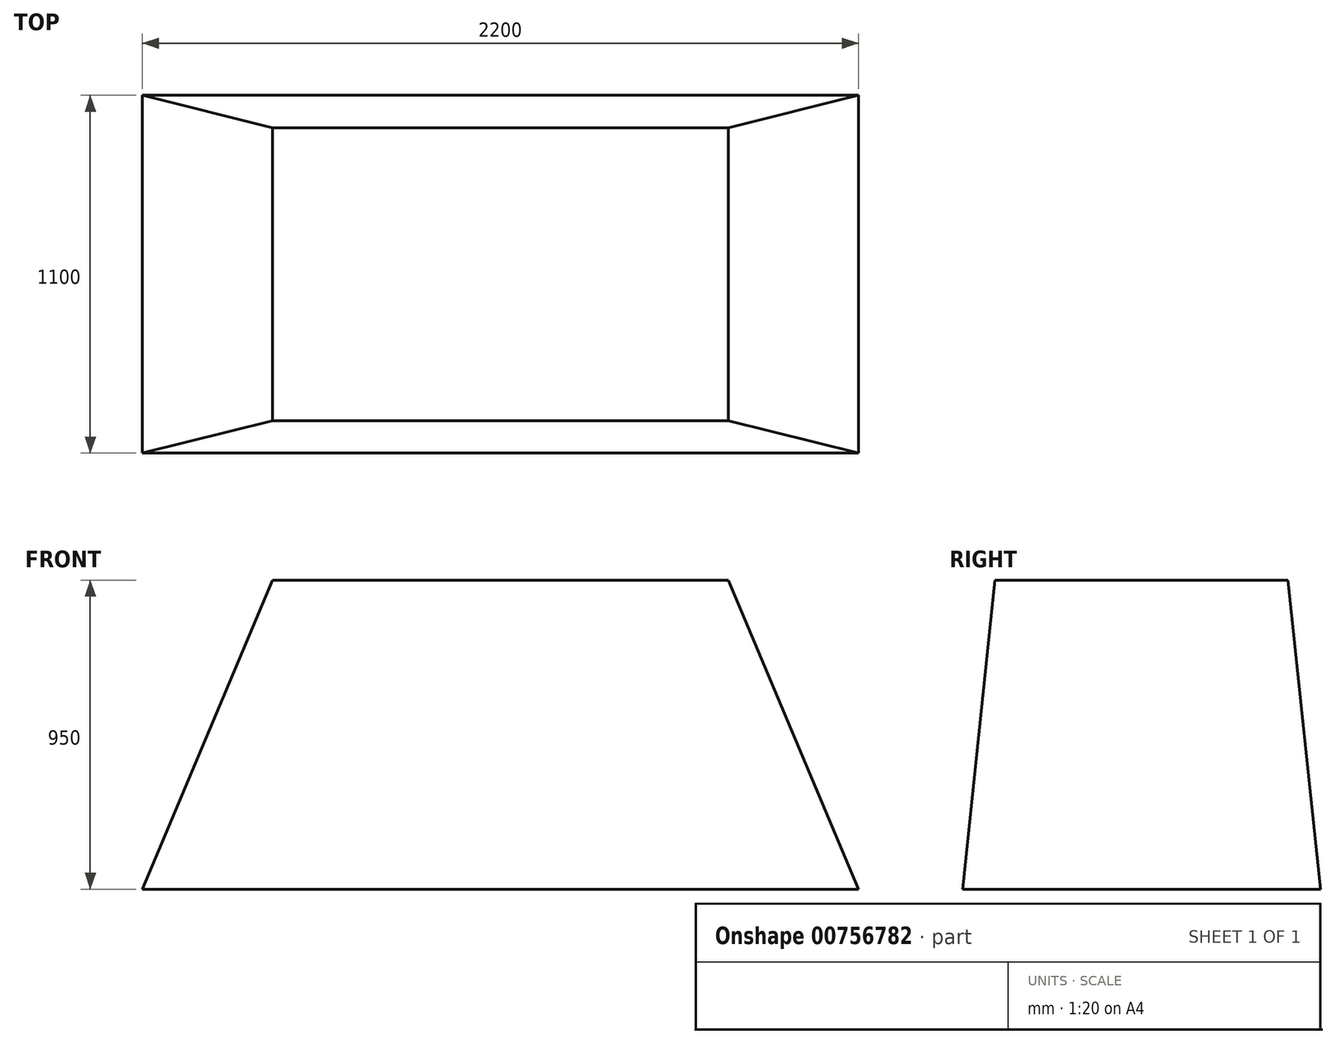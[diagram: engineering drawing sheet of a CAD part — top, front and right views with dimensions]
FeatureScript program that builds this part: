
annotation { "Feature Type Name" : "Feature", "Feature Type Description" : "" }
export const myFeature = defineFeature(function(context is Context, id is Id, definition is map)
    precondition{}
    {
        {
            var Q0;
            Q0=qCreatedBy(makeId("Front.planeOp"),FACE);
            var sketch = newSketch(context, id + "F0", { "sketchPlane" : qUnion([Q0])});
            skLineSegment(sketch, "E0", {"start": v(0, 0) * mm, "end": v(2200, 0) * mm});
            skLineSegment(sketch, "E1", {"start": v(2200, 0) * mm, "end": v(1800, 950) * mm});
            skLineSegment(sketch, "E2", {"start": v(1800, 950) * mm, "end": v(400, 950) * mm});
            skLineSegment(sketch, "E3", {"start": v(400, 950) * mm, "end": v(0, 0) * mm});
            skSolve(sketch);
        }
        {
            var Q0;
            Q0=makeQuery(id+"F0.imprint","IMPRINT",FACE,{"disambiguationData":[TD([[makeQuery(id+"F0.imprint","IMPRINT",EDGE,{"derivedFrom":sQuery(id+"F0.wireOp",EDGE,"E0")}),1.0]])]});
            extrude(context, id + "F1", {"entities" : qUnion([Q0]), "endBound" : BoundingType.SYMMETRIC, "depth" : 1100 * mm, "offsetDistance" : 25 * mm});
        }
        {
            var Q0;
            Q0=qCreatedBy(makeId("Right.planeOp"),FACE);
            var sketch = newSketch(context, id + "F2", { "sketchPlane" : qUnion([Q0])});
            skLineSegment(sketch, "E4.0", {"start": v(-550, 0) * mm, "end": v(550, 0) * mm});
            skLineSegment(sketch, "E5.0", {"start": v(-550, 950) * mm, "end": v(550, 950) * mm});
            skLineSegment(sketch, "E6.0", {"start": v(-550, 0) * mm, "end": v(-550, 950) * mm});
            skLineSegment(sketch, "E7.0", {"start": v(550, 0) * mm, "end": v(550, 950) * mm});
            skLineSegment(sketch, "E8", {"start": v(-550, 0) * mm, "end": v(-450, 950) * mm});
            skLineSegment(sketch, "E9", {"start": v(550, 0) * mm, "end": v(450, 950) * mm});
            skSolve(sketch);
        }
        {
            var Q0;
            {var subQ0=sQuery(id+"F2.wireOp",EDGE,"E6.0");Q0=makeQuery(id+"F2.imprint","IMPRINT",FACE,{"disambiguationData":[TD([[makeQuery(id+"F2.imprint","IMPRINT",EDGE,{"derivedFrom":subQ0}),-1.0]])]});}
            var Q1;
            {var subQ0=sQuery(id+"F2.wireOp",EDGE,"E7.0");Q1=makeQuery(id+"F2.imprint","IMPRINT",FACE,{"disambiguationData":[TD([[makeQuery(id+"F2.imprint","IMPRINT",EDGE,{"derivedFrom":subQ0}),1.0]])]});}
            extrude(context, id + "F3", {"entities" : qUnion([Q0, Q1]), "operationType" : NewBodyOperationType.REMOVE, "endBound" : BoundingType.THROUGH_ALL, "depth" : 25 * mm, "offsetDistance" : 25 * mm});
        }
    });
